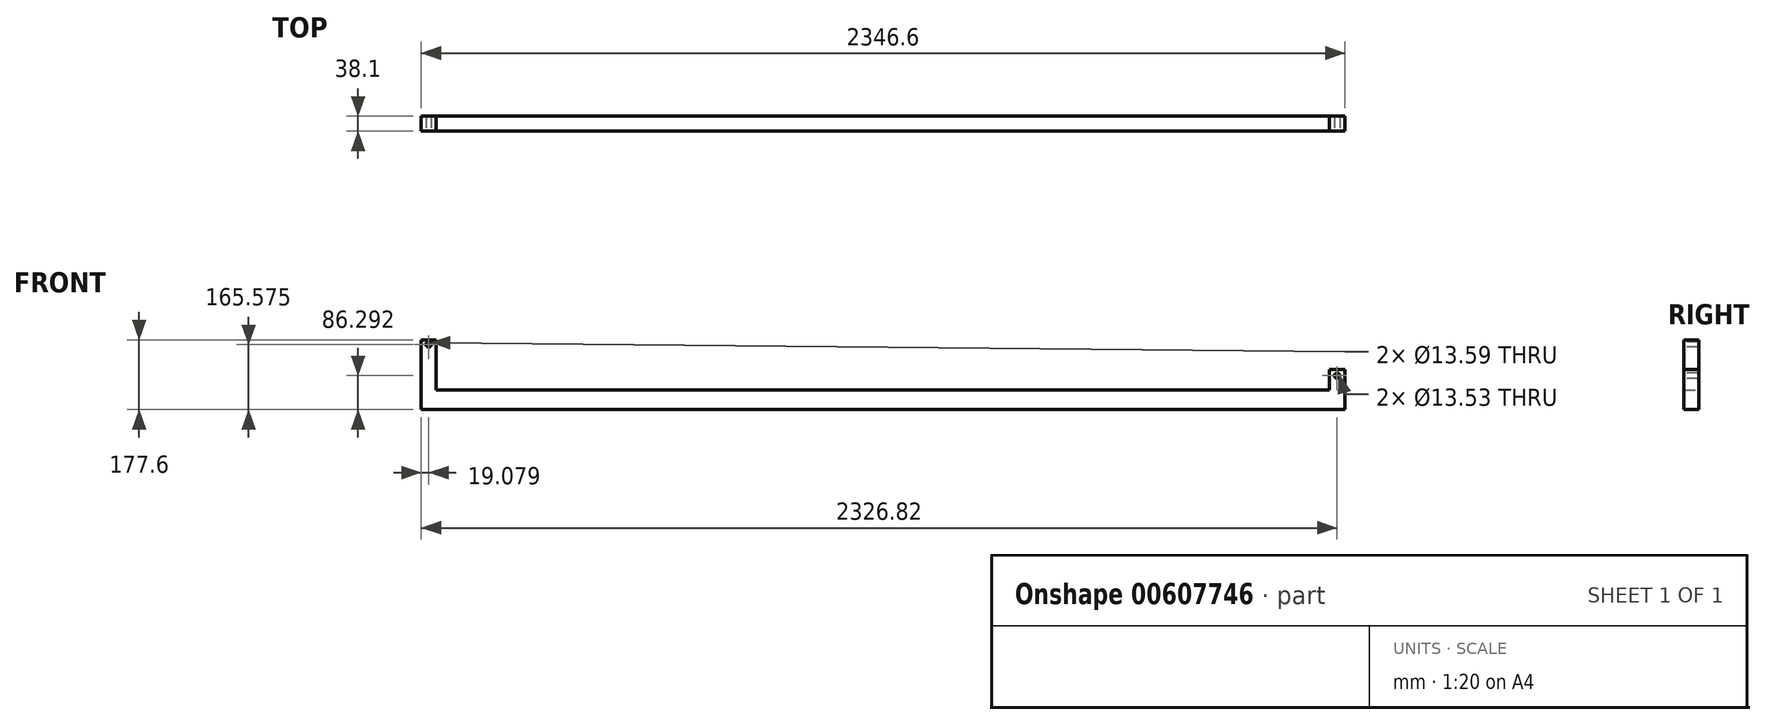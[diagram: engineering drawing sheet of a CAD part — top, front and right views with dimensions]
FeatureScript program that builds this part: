
annotation { "Feature Type Name" : "Feature", "Feature Type Description" : "" }
export const myFeature = defineFeature(function(context is Context, id is Id, definition is map)
    precondition{}
    {
        {
            var Q0;
            Q0=qCreatedBy(makeId("Front.planeOp"),FACE);
            var sketch = newSketch(context, id + "F0", { "sketchPlane" : qUnion([Q0])});
            skLineSegment(sketch, "E0.bottom", {"start": v(-201.36, -16.64) * mm, "end": v(201.36, -16.64) * mm});
            skLineSegment(sketch, "E0.top", {"start": v(-201.36, 16.64) * mm, "end": v(201.36, 16.64) * mm});
            skLineSegment(sketch, "E0.left", {"start": v(-201.36, -16.64) * mm, "end": v(-201.36, 16.64) * mm});
            skLineSegment(sketch, "E0.right", {"start": v(201.36, -16.64) * mm, "end": v(201.36, 16.64) * mm});
            skPoint(sketch, "E0.middle", {"position": v(0, 0) * mm});
            skCircle(sketch, "E1", {"center": v(-185.64, 0) * mm, "radius": 5.62 * mm});
            skCircle(sketch, "E2", {"center": v(89.5, 0) * mm, "radius": 6.48 * mm});
            skSolve(sketch);
        }
        {
            var Q0;
            Q0=makeQuery(id+"F0.imprint","IMPRINT",FACE,{"disambiguationData":[TD([[makeQuery(id+"F0.imprint","IMPRINT",EDGE,{"derivedFrom":sQuery(id+"F0.wireOp",EDGE,"E0.bottom")}),1.0]])]});
            extrude(context, id + "F1", {"entities" : qUnion([Q0]), "depth" : 38.1 * mm, "offsetDistance" : 25.4 * mm});
        }
        {
            var Q0;
            Q0=makeQuery(id+"F1.opExtrude","CAP_FACE",FACE,{"disambiguationData":[OSD([sQuery(id+"F0.wireOp",EDGE,"E0.bottom"),sQuery(id+"F0.wireOp",EDGE,"E0.top"),sQuery(id+"F0.wireOp",EDGE,"E0.left"),sQuery(id+"F0.wireOp",EDGE,"E0.right"),sQuery(id+"F0.wireOp",EDGE,"E1"),sQuery(id+"F0.wireOp",EDGE,"E2")])],"isStart":true});
            var sketch = newSketch(context, id + "F2", { "sketchPlane" : qUnion([Q0])});
            skLineSegment(sketch, "E3.bottom", {"start": v(201.36, 16.64) * mm, "end": v(163.25, 16.64) * mm});
            skLineSegment(sketch, "E3.top", {"start": v(201.36, 80.92) * mm, "end": v(163.25, 80.92) * mm});
            skLineSegment(sketch, "E3.left", {"start": v(201.36, 16.64) * mm, "end": v(201.36, 80.92) * mm});
            skLineSegment(sketch, "E3.right", {"start": v(163.25, 16.64) * mm, "end": v(163.25, 80.92) * mm});
            skLineSegment(sketch, "E4.bottom", {"start": v(-201.36, 16.64) * mm, "end": v(-163, 16.64) * mm});
            skLineSegment(sketch, "E4.top", {"start": v(-201.36, 54.7) * mm, "end": v(-163, 54.7) * mm});
            skLineSegment(sketch, "E4.left", {"start": v(-201.36, 16.64) * mm, "end": v(-201.36, 54.7) * mm});
            skLineSegment(sketch, "E4.right", {"start": v(-163, 16.64) * mm, "end": v(-163, 54.7) * mm});
            skSolve(sketch);
        }
        {
            var Q0;
            Q0=makeQuery(id+"F2.imprint","IMPRINT",FACE,{"disambiguationData":[TD([[makeQuery(id+"F2.imprint","IMPRINT",EDGE,{"derivedFrom":sQuery(id+"F2.wireOp",EDGE,"E4.bottom")}),-1.0]])]});
            var Q1;
            Q1=makeQuery(id+"F2.imprint","IMPRINT",FACE,{"disambiguationData":[TD([[makeQuery(id+"F2.imprint","IMPRINT",EDGE,{"derivedFrom":sQuery(id+"F2.wireOp",EDGE,"E3.bottom")}),-1.0]])]});
            extrude(context, id + "F3", {"entities" : qUnion([Q0, Q1]), "operationType" : NewBodyOperationType.ADD, "depth" : -38.1 * mm, "offsetDistance" : 25.4 * mm});
        }
        {
            var Q0;
            Q0=makeQuery(id+"F1.opExtrude","SWEPT_BODY",BODY,{"disambiguationData":[OSD([sQuery(id+"F0.wireOp",EDGE,"E0.bottom"),sQuery(id+"F0.wireOp",EDGE,"E0.top"),sQuery(id+"F0.wireOp",EDGE,"E0.left"),sQuery(id+"F0.wireOp",EDGE,"E0.right"),sQuery(id+"F0.wireOp",EDGE,"E1"),sQuery(id+"F0.wireOp",EDGE,"E2")])]});
            deleteBodies(context, id + "F4", {"entities" : qUnion([Q0])});
        }
        {
            var Q0;
            Q0=qCreatedBy(makeId("Front.planeOp"),FACE);
            var sketch = newSketch(context, id + "F5", { "sketchPlane" : qUnion([Q0])});
            skLineSegment(sketch, "E5.bottom", {"start": v(-1173.3, 24.83) * mm, "end": v(1173.3, 24.83) * mm});
            skLineSegment(sketch, "E5.top", {"start": v(-1173.3, -24.83) * mm, "end": v(1173.3, -24.83) * mm});
            skLineSegment(sketch, "E5.left", {"start": v(-1173.3, 24.83) * mm, "end": v(-1173.3, -24.83) * mm});
            skLineSegment(sketch, "E5.right", {"start": v(1173.3, 24.83) * mm, "end": v(1173.3, -24.83) * mm});
            skPoint(sketch, "E5.middle", {"position": v(0, 0) * mm});
            skLineSegment(sketch, "E6.bottom", {"start": v(-1173.3, 24.83) * mm, "end": v(-1135.14, 24.83) * mm});
            skLineSegment(sketch, "E6.top", {"start": v(-1173.3, 152.77) * mm, "end": v(-1135.14, 152.77) * mm});
            skLineSegment(sketch, "E6.left", {"start": v(-1173.3, 24.83) * mm, "end": v(-1173.3, 152.77) * mm});
            skLineSegment(sketch, "E6.right", {"start": v(-1135.14, 24.83) * mm, "end": v(-1135.14, 152.77) * mm});
            skLineSegment(sketch, "E7.bottom", {"start": v(1173.3, 24.83) * mm, "end": v(1133.74, 24.83) * mm});
            skLineSegment(sketch, "E7.top", {"start": v(1173.3, 76.74) * mm, "end": v(1133.74, 76.74) * mm});
            skLineSegment(sketch, "E7.left", {"start": v(1173.3, 24.83) * mm, "end": v(1173.3, 76.74) * mm});
            skLineSegment(sketch, "E7.right", {"start": v(1133.74, 24.83) * mm, "end": v(1133.74, 76.74) * mm});
            skSolve(sketch);
        }
        {
            var Q0;
            Q0 = qSketchRegion(id + "F5", true);
            extrude(context, id + "F6", {"entities" : qUnion([Q0]), "depth" : 38.1 * mm, "offsetDistance" : 25.4 * mm});
        }
        {
            var Q0;
            Q0=makeQuery(id+"F6.opExtrude","CAP_FACE",FACE,{"disambiguationData":[OSD([sQuery(id+"F5.wireOp",EDGE,"E5.bottom"),sQuery(id+"F5.wireOp",EDGE,"E5.top"),sQuery(id+"F5.wireOp",EDGE,"E5.left"),sQuery(id+"F5.wireOp",EDGE,"E5.right"),sQuery(id+"F5.wireOp",EDGE,"E6.top"),sQuery(id+"F5.wireOp",EDGE,"E6.left"),sQuery(id+"F5.wireOp",EDGE,"E6.right"),sQuery(id+"F5.wireOp",EDGE,"E7.top"),sQuery(id+"F5.wireOp",EDGE,"E7.left"),sQuery(id+"F5.wireOp",EDGE,"E7.right")])],"isStart":false});
            var sketch = newSketch(context, id + "F7", { "sketchPlane" : qUnion([Q0])});
            skCircle(sketch, "E8", {"center": v(-1154.22, 140.75) * mm, "radius": 6.8 * mm});
            skPoint(sketch, "E8.centerSnap0", {"position": v(-1154.22, 152.77) * mm});
            skCircle(sketch, "E9", {"center": v(1153.52, 63.35) * mm, "radius": 6.84 * mm});
            skPoint(sketch, "E9.centerSnap0", {"position": v(1153.52, 76.74) * mm});
            skSolve(sketch);
        }
        {
            var Q0;
            Q0=makeQuery(id+"F7.imprint","IMPRINT",FACE,{"disambiguationData":[TD([[makeQuery(id+"F7.imprint","IMPRINT",EDGE,{"derivedFrom":sQuery(id+"F7.wireOp",EDGE,"E8")}),1.0]])]});
            extrude(context, id + "F8", {"entities" : qUnion([Q0]), "operationType" : NewBodyOperationType.REMOVE, "oppositeDirection" : true, "depth" : 38.1 * mm, "offsetDistance" : 25.4 * mm});
        }
        {
            var Q0;
            Q0=makeQuery(id+"F6.opExtrude","CAP_FACE",FACE,{"disambiguationData":[OSD([sQuery(id+"F5.wireOp",EDGE,"E5.bottom"),sQuery(id+"F5.wireOp",EDGE,"E5.top"),sQuery(id+"F5.wireOp",EDGE,"E5.left"),sQuery(id+"F5.wireOp",EDGE,"E5.right"),sQuery(id+"F5.wireOp",EDGE,"E6.top"),sQuery(id+"F5.wireOp",EDGE,"E6.left"),sQuery(id+"F5.wireOp",EDGE,"E6.right"),sQuery(id+"F5.wireOp",EDGE,"E7.top"),sQuery(id+"F5.wireOp",EDGE,"E7.left"),sQuery(id+"F5.wireOp",EDGE,"E7.right")])],"isStart":false});
            var sketch = newSketch(context, id + "F9", { "sketchPlane" : qUnion([Q0])});
            skCircle(sketch, "E10", {"center": v(1153.52, 61.46) * mm, "radius": 6.77 * mm});
            skPoint(sketch, "E10.centerSnap0", {"position": v(1153.52, 76.74) * mm});
            skSolve(sketch);
        }
        {
            var Q0;
            Q0=makeQuery(id+"F9.imprint","IMPRINT",FACE,{"disambiguationData":[TD([[makeQuery(id+"F9.imprint","IMPRINT",EDGE,{"derivedFrom":sQuery(id+"F9.wireOp",EDGE,"E10")}),1.0]])]});
            extrude(context, id + "F10", {"entities" : qUnion([Q0]), "operationType" : NewBodyOperationType.REMOVE, "oppositeDirection" : true, "depth" : 38.1 * mm, "offsetDistance" : 25.4 * mm});
        }
        {
            var Q0;
            Q0=makeQuery(id+"F6.opExtrude","SWEPT_BODY",BODY,{"disambiguationData":[OSD([sQuery(id+"F5.wireOp",EDGE,"E5.bottom"),sQuery(id+"F5.wireOp",EDGE,"E5.top"),sQuery(id+"F5.wireOp",EDGE,"E5.left"),sQuery(id+"F5.wireOp",EDGE,"E5.right"),sQuery(id+"F5.wireOp",EDGE,"E6.top"),sQuery(id+"F5.wireOp",EDGE,"E6.left"),sQuery(id+"F5.wireOp",EDGE,"E6.right"),sQuery(id+"F5.wireOp",EDGE,"E7.top"),sQuery(id+"F5.wireOp",EDGE,"E7.left"),sQuery(id+"F5.wireOp",EDGE,"E7.right")])]});
            transform(context, id + "F11", {"entities" : qUnion([Q0]), "transformType" : TransformType.TRANSLATION_3D, "dx" : 0 * mm, "dy" : 0 * mm, "dz" : 0 * mm, "makeCopy" : true});
        }
    });
